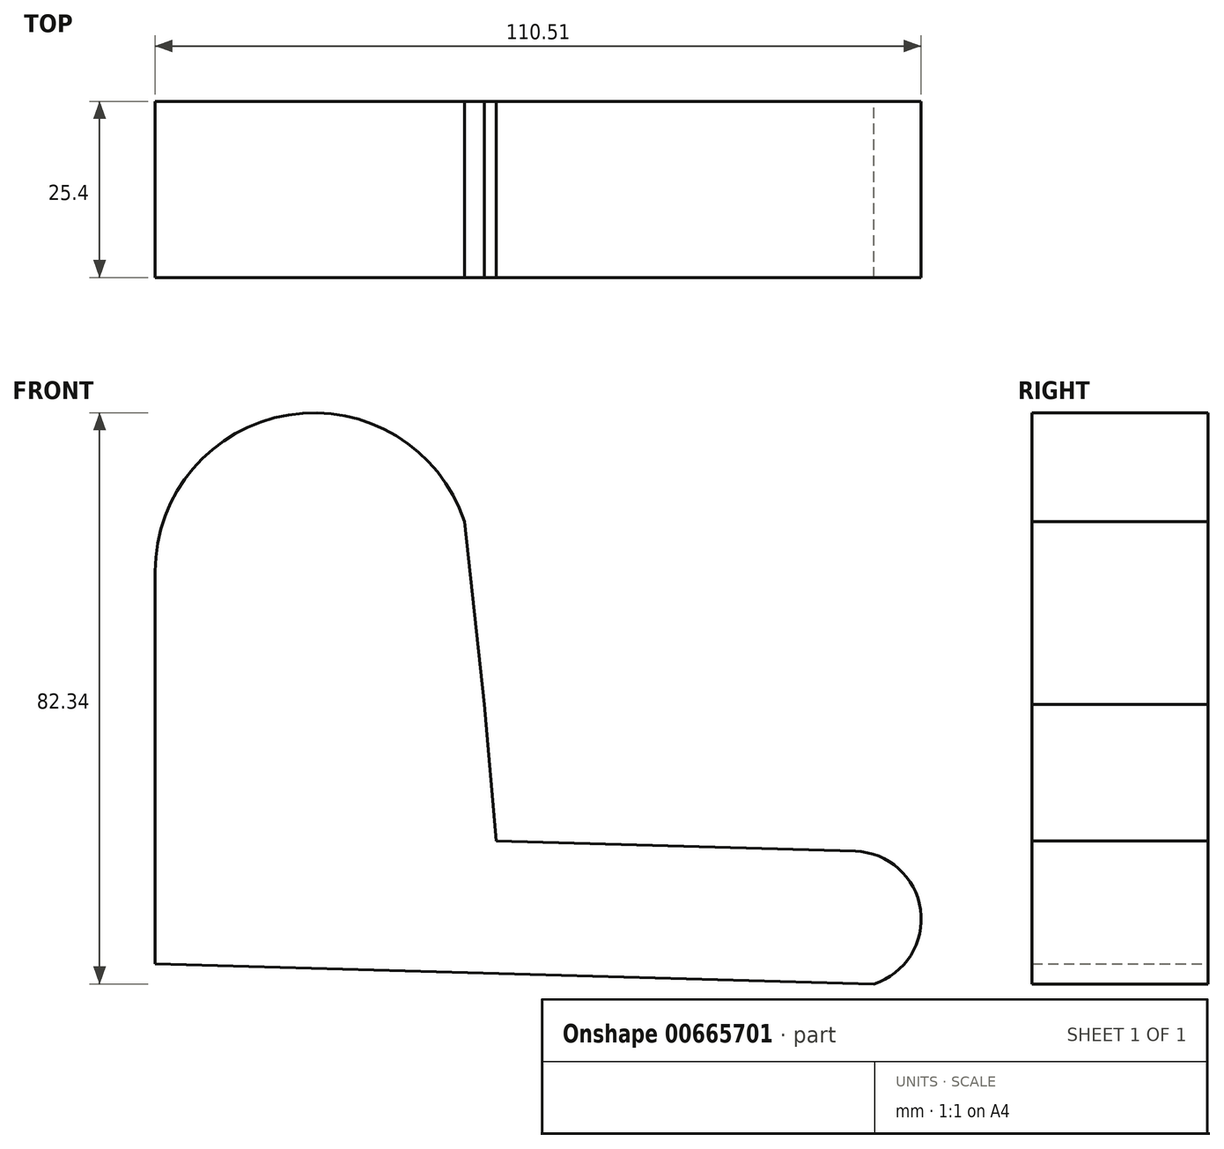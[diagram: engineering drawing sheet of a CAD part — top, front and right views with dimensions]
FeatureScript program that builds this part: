
annotation { "Feature Type Name" : "Feature", "Feature Type Description" : "" }
export const myFeature = defineFeature(function(context is Context, id is Id, definition is map)
    precondition{}
    {
        {
            var Q0;
            Q0=qCreatedBy(makeId("Front.planeOp"),FACE);
            var sketch = newSketch(context, id + "F0", { "sketchPlane" : qUnion([Q0])});
            skLineSegment(sketch, "E0", {"start": v(-53.17, -27.66) * mm, "end": v(-53.17, 12.44) * mm});
            skArc(sketch, "E1", {"start": v(-8.54, 19.64) * mm, "mid": v(-33.92, 35.05) * mm, "end": v(-53.17, 12.44) * mm});
            skLineSegment(sketch, "E2", {"start": v(-8.54, 19.64) * mm, "end": v(-5.66, -6.68) * mm});
            skLineSegment(sketch, "E3", {"start": v(-5.66, -6.68) * mm, "end": v(-3.97, -26.4) * mm});
            skLineSegment(sketch, "E4", {"start": v(-3.97, -26.4) * mm, "end": v(47.82, -27.87) * mm});
            skLineSegment(sketch, "E5", {"start": v(-53.17, -27.66) * mm, "end": v(-53.17, -44.12) * mm});
            skArc(sketch, "E6", {"start": v(50.5, -47) * mm, "mid": v(57.24, -36.3) * mm, "end": v(47.82, -27.87) * mm});
            skLineSegment(sketch, "E7", {"start": v(50.5, -47) * mm, "end": v(-53.17, -44.12) * mm});
            skSolve(sketch);
        }
        {
            var Q0;
            Q0 = qSketchRegion(id + "F0", true);
            extrude(context, id + "F1", {"entities" : qUnion([Q0]), "depth" : 25.4 * mm, "offsetDistance" : 25.4 * mm});
        }
    });
